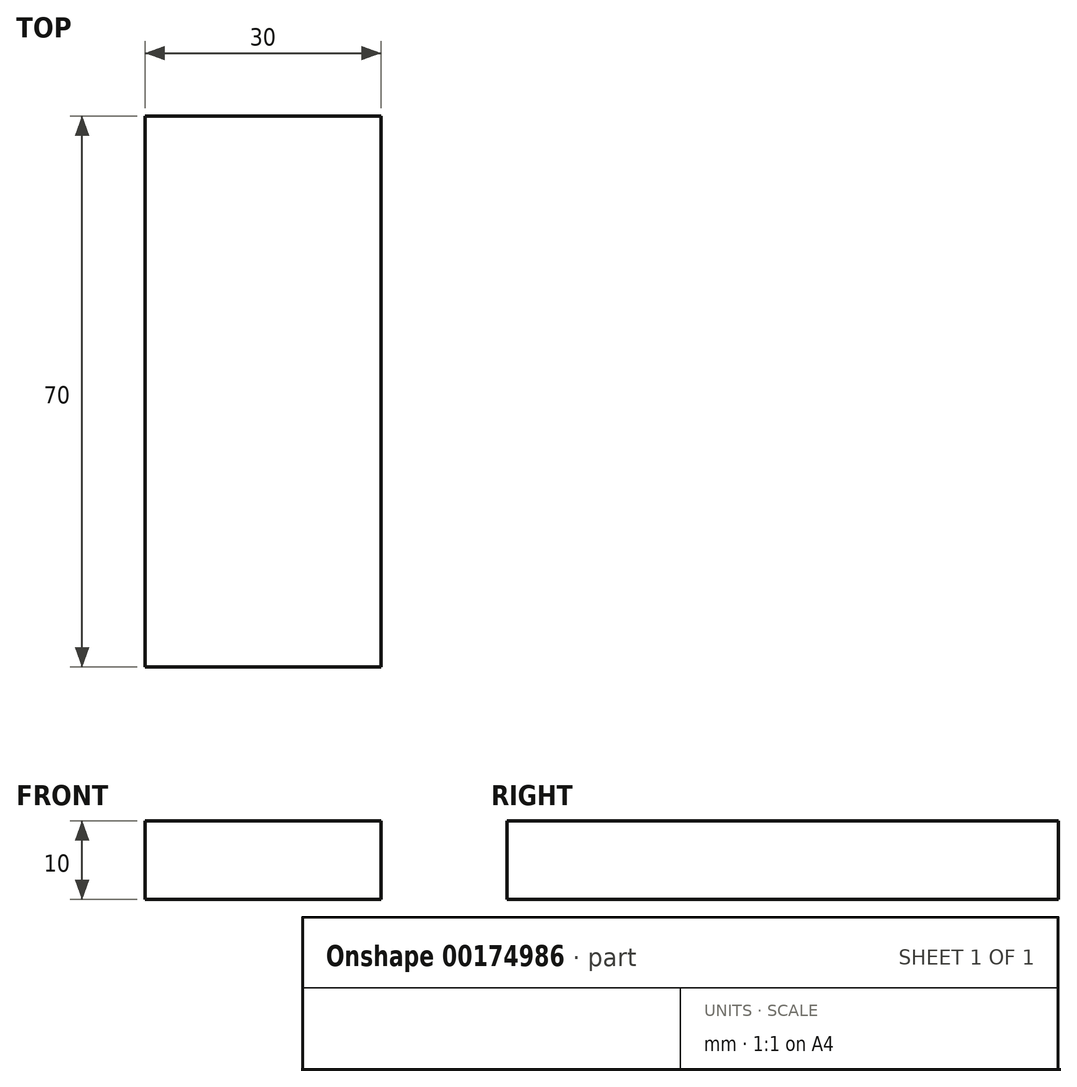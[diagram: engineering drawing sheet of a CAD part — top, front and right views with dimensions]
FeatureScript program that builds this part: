
annotation { "Feature Type Name" : "Feature", "Feature Type Description" : "" }
export const myFeature = defineFeature(function(context is Context, id is Id, definition is map)
    precondition{}
    {
        {
            var Q0;
            Q0=qCreatedBy(makeId("Top.planeOp"),FACE);
            var sketch = newSketch(context, id + "F0", { "sketchPlane" : qUnion([Q0])});
            skLineSegment(sketch, "E0.bottom", {"start": v(15, -35) * mm, "end": v(-15, -35) * mm});
            skLineSegment(sketch, "E0.top", {"start": v(15, 35) * mm, "end": v(-15, 35) * mm});
            skLineSegment(sketch, "E0.left", {"start": v(15, -35) * mm, "end": v(15, 35) * mm});
            skLineSegment(sketch, "E0.right", {"start": v(-15, -35) * mm, "end": v(-15, 35) * mm});
            skPoint(sketch, "E0.middle", {"position": v(0, 0) * mm});
            skSolve(sketch);
        }
        {
            var Q0;
            Q0=makeQuery(id+"F0.imprint","IMPRINT",FACE,{"disambiguationData":[TD([[makeQuery(id+"F0.imprint","IMPRINT",EDGE,{"derivedFrom":sQuery(id+"F0.wireOp",EDGE,"E0.bottom")}),-1.0]])]});
            extrude(context, id + "F1", {"entities" : qUnion([Q0]), "depth" : 10 * mm});
        }
    });
